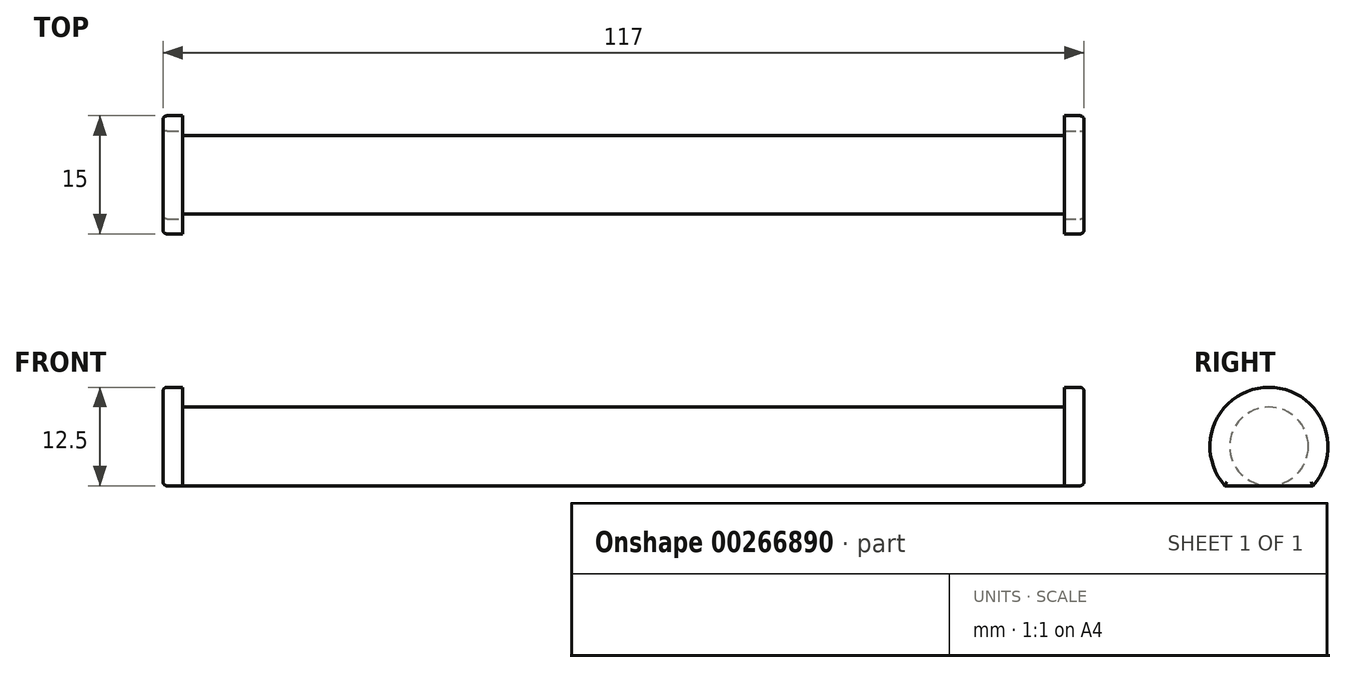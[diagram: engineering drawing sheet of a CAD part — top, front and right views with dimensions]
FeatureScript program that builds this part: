
annotation { "Feature Type Name" : "Feature", "Feature Type Description" : "" }
export const myFeature = defineFeature(function(context is Context, id is Id, definition is map)
    precondition{}
    {
        {
            var Q0;
            Q0=qCreatedBy(makeId("Right.planeOp"),FACE);
            var sketch = newSketch(context, id + "F0", { "sketchPlane" : qUnion([Q0])});
            skCircle(sketch, "E0", {"center": v(0, 0) * mm, "radius": 5 * mm});
            skSolve(sketch);
        }
        {
            var Q0;
            Q0 = qSketchRegion(id + "F0", true);
            extrude(context, id + "F1", {"entities" : qUnion([Q0]), "depth" : 112 * mm});
        }
        {
            var Q0;
            Q0=makeQuery(id+"F1.opExtrude","CAP_FACE",FACE,{"disambiguationData":[OSD([sQuery(id+"F0.wireOp",EDGE,"E0")])],"isStart":true});
            var sketch = newSketch(context, id + "F2", { "sketchPlane" : qUnion([Q0])});
            skCircle(sketch, "E1", {"center": v(0, 0) * mm, "radius": 7.5 * mm});
            skSolve(sketch);
        }
        {
            var Q0;
            Q0 = qSketchRegion(id + "F2", true);
            extrude(context, id + "F3", {"entities" : qUnion([Q0]), "operationType" : NewBodyOperationType.ADD, "depth" : 2.5 * mm});
        }
        {
            var Q0;
            Q0=makeQuery(id+"F1.opExtrude","CAP_FACE",FACE,{"disambiguationData":[OSD([sQuery(id+"F0.wireOp",EDGE,"E0")])],"isStart":false});
            var sketch = newSketch(context, id + "F4", { "sketchPlane" : qUnion([Q0])});
            skCircle(sketch, "E2", {"center": v(0, 0) * mm, "radius": 7.5 * mm});
            skSolve(sketch);
        }
        {
            var Q0;
            Q0 = qSketchRegion(id + "F4", true);
            extrude(context, id + "F5", {"entities" : qUnion([Q0]), "operationType" : NewBodyOperationType.ADD, "depth" : 2.5 * mm});
        }
        {
            var Q0;
            Q0=makeQuery(id+"F5.opExtrude","CAP_FACE",FACE,{"disambiguationData":[OSD([sQuery(id+"F4.wireOp",EDGE,"E2")])],"isStart":false});
            var sketch = newSketch(context, id + "F6", { "sketchPlane" : qUnion([Q0])});
            skArc(sketch, "E3.0", {"start": v(-5.6, -5) * mm, "mid": v(0, -7.5) * mm, "end": v(5.6, -5) * mm});
            skLineSegment(sketch, "E4", {"start": v(-5.6, -5) * mm, "end": v(5.6, -5) * mm});
            skSolve(sketch);
        }
        {
            var Q0;
            Q0 = qSketchRegion(id + "F6", true);
            extrude(context, id + "F7", {"entities" : qUnion([Q0]), "operationType" : NewBodyOperationType.REMOVE, "endBound" : BoundingType.THROUGH_ALL, "oppositeDirection" : true, "depth" : 25 * mm});
        }
        {
            var Q0;
            Q0=makeQuery(id+"F3.opExtrude","CAP_FACE",FACE,{"disambiguationData":[OSD([sQuery(id+"F2.wireOp",EDGE,"E1")])],"isStart":false});
            var Q1;
            Q1=makeQuery(id+"F5.opExtrude","CAP_FACE",FACE,{"disambiguationData":[OSD([sQuery(id+"F4.wireOp",EDGE,"E2")])],"isStart":false});
            var Q2;
            {var subQ0=sQuery(id+"F4.wireOp",EDGE,"E2");var subQ1=sQuery(id+"F6.wireOp",EDGE,"E4");var subQ2=sQuery(id+"F6.wireOp",EDGE,"E3.0");Q2=makeQuery(id+"F7.boolean.opBoolean","COPY",EDGE,{"disambiguationData":[topologyDisambiguationEdgeConnected([makeQuery(id+"F5.opExtrude","SWEPT_FACE",FACE,{"disambiguationData":[OSD([subQ0])]})])],"derivedFrom":makeQuery(id+"F7.opExtrude","SWEPT_EDGE",EDGE,{"disambiguationData":[OSD([subQ0,subQ2,subQ1]),TDD([makeQuery(id+"F6.imprint","INTERSECT",VERTEX,{"disambiguationData":[OD(0.0)],"derivedFrom":[makeQuery(id+"F5.opExtrude","CAP_EDGE",EDGE,{"disambiguationData":[OSD([subQ0])],"isStart":false}),subQ2,subQ1]})])]})});}
            var Q3;
            {var subQ0=sQuery(id+"F4.wireOp",EDGE,"E2");var subQ1=sQuery(id+"F6.wireOp",EDGE,"E4");var subQ2=sQuery(id+"F6.wireOp",EDGE,"E3.0");Q3=makeQuery(id+"F7.boolean.opBoolean","COPY",EDGE,{"disambiguationData":[topologyDisambiguationEdgeConnected([makeQuery(id+"F5.opExtrude","SWEPT_FACE",FACE,{"disambiguationData":[OSD([subQ0])]})])],"derivedFrom":makeQuery(id+"F7.opExtrude","SWEPT_EDGE",EDGE,{"disambiguationData":[OSD([subQ0,subQ2,subQ1]),TDD([makeQuery(id+"F6.imprint","INTERSECT",VERTEX,{"disambiguationData":[OD(1.0)],"derivedFrom":[makeQuery(id+"F5.opExtrude","CAP_EDGE",EDGE,{"disambiguationData":[OSD([subQ0])],"isStart":false}),subQ2,subQ1]})])]})});}
            var Q4;
            {var subQ0=sQuery(id+"F6.wireOp",EDGE,"E4");var subQ1=sQuery(id+"F6.wireOp",EDGE,"E3.0");var subQ2=sQuery(id+"F4.wireOp",EDGE,"E2");Q4=makeQuery(id+"F7.boolean.opBoolean","COPY",EDGE,{"disambiguationData":[topologyDisambiguationEdgeConnected([makeQuery(id+"F3.opExtrude","SWEPT_FACE",FACE,{"disambiguationData":[OSD([sQuery(id+"F2.wireOp",EDGE,"E1")])]})])],"derivedFrom":makeQuery(id+"F7.opExtrude","SWEPT_EDGE",EDGE,{"disambiguationData":[OSD([subQ2,subQ1,subQ0]),TDD([makeQuery(id+"F6.imprint","INTERSECT",VERTEX,{"disambiguationData":[OD(0.0)],"derivedFrom":[makeQuery(id+"F5.opExtrude","CAP_EDGE",EDGE,{"disambiguationData":[OSD([subQ2])],"isStart":false}),subQ1,subQ0]})])]})});}
            var Q5;
            {var subQ0=sQuery(id+"F6.wireOp",EDGE,"E4");var subQ1=sQuery(id+"F6.wireOp",EDGE,"E3.0");var subQ2=sQuery(id+"F4.wireOp",EDGE,"E2");Q5=makeQuery(id+"F7.boolean.opBoolean","COPY",EDGE,{"disambiguationData":[topologyDisambiguationEdgeConnected([makeQuery(id+"F3.opExtrude","SWEPT_FACE",FACE,{"disambiguationData":[OSD([sQuery(id+"F2.wireOp",EDGE,"E1")])]})])],"derivedFrom":makeQuery(id+"F7.opExtrude","SWEPT_EDGE",EDGE,{"disambiguationData":[OSD([subQ2,subQ1,subQ0]),TDD([makeQuery(id+"F6.imprint","INTERSECT",VERTEX,{"disambiguationData":[OD(1.0)],"derivedFrom":[makeQuery(id+"F5.opExtrude","CAP_EDGE",EDGE,{"disambiguationData":[OSD([subQ2])],"isStart":false}),subQ1,subQ0]})])]})});}
            fillet(context, id + "F8", {"entities" : qUnion([Q0, Q1, Q2, Q3, Q4, Q5]), "radius" : 0.5 * mm, "tangentPropagation" : true, "allowEdgeOverflow" : false});
        }
    });
